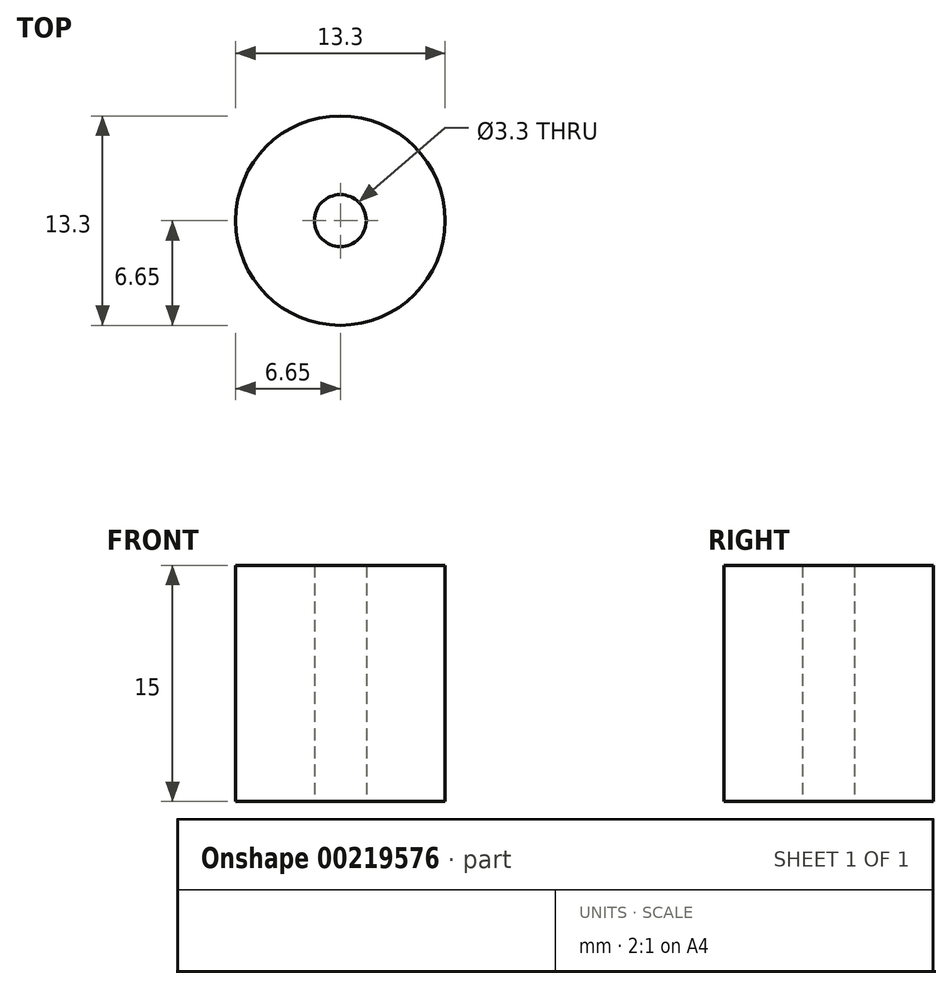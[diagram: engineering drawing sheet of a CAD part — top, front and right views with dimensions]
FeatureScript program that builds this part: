
annotation { "Feature Type Name" : "Feature", "Feature Type Description" : "" }
export const myFeature = defineFeature(function(context is Context, id is Id, definition is map)
    precondition{}
    {
        {
            var Q0;
            Q0=qCreatedBy(makeId("Top.planeOp"),FACE);
            var sketch = newSketch(context, id + "F0", { "sketchPlane" : qUnion([Q0])});
            skCircle(sketch, "E0", {"center": v(0, 0) * mm, "radius": 1.65 * mm});
            skCircle(sketch, "E1", {"center": v(0, 0) * mm, "radius": 6.65 * mm});
            skSolve(sketch);
        }
        {
            var Q0;
            Q0 = qSketchRegion(id + "F0", true);
            extrude(context, id + "F1", {"entities" : qUnion([Q0]), "depth" : 15 * mm});
        }
    });
